# Revit family: ESC 90 LED EMERGENCY EXIT LIGHT TWS9092WM
name_source: partatom
category: Electrical Fixtures
revit_build: Autodesk Revit 2015 (Build: 20160512_0715(x64)
units: mm (PartAtom-declared; Revit-internal decimal feet)

## types (4) — shared parameters
Depth = 40 mm  [stored 0.131234 ft]
Height = 202 mm  [stored 0.66273 ft]
Manufacturer = Teknoware Oy
Model = ESC 90
Product Code = TWS9092WA
Viewing Distance = 25000 mm
Width = 268 mm

## per-type parameters (varying)
| type | Back Pictogram | Down Arrow | Front Pictogram | Left Arrow | Right Arrow | Type Comments | Up Arrow |
| -arrow left | Teknoware Pictogram PB9005 | No | Teknoware Pictogram PB9004 | Yes | No | PB9004 | No |
| -arrow right | Teknoware Pictogram PB9004 | No | Teknoware Pictogram PB9005 | No | Yes | PB9005 | No |
| -arrow down | Teknoware Pictogram PB9006 | Yes | Teknoware Pictogram PB9006 | No | No | PB9006 | No |
| -arrow up | Teknoware Pictogram PB9010 | No | Teknoware Pictogram PB9010 | No | No | PB9010 | Yes |

note: [stored X ft] marks values corroborated as IEEE doubles in the binary element streams (Revit-internal decimal feet)

## geometry (parser evidence)
native form markers: Blend x6, Sweep x14
no freeform markers — native parametric forms only
